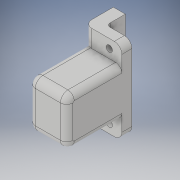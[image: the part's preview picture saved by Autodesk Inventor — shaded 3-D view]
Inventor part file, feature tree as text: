
AUTODESK INVENTOR PART (.ipt)
format: ipt  version: 2019 (Build 230136000, 136)  size: 225,792 bytes
history: native  units: in
note: dims shown in document units (in); Inventor stores cm internally (conversion verified against a paired STEP export)
features: sketch x7, extrude x5, fillet x3, hole x2
ambient origin geometry x8: Origin, YZ Plane, XZ Plane, XY Plane, X Axis, Y Axis, Z Axis, Center Point
bodies: Solid1 (feature_tree)
feature tree (17):
  extrude  "Extrusion1"  Depth=0.75in
  extrude  "Extrusion2"  Depth=0.38in TaperAngle=0.0deg
  extrude  "Extrusion3"  Depth=1.645in
  extrude  "Extrusion4"  Depth=0.35in
  extrude  "Extrusion5"  Depth=0.6in TaperAngle=0.0deg
  hole  "Hole1"  [1 undecoded]
  hole  "Hole2"  [1 undecoded]
  fillet  "Fillet1"  Radius=0.25in
  fillet  "Fillet2"  Radius=0.19in
  fillet  "Fillet3"  Radius=0.19in
  sketch  "Sketch2"  dims[d2=0.75in d3=1.645in]
  sketch  "Sketch3"  dims[d4=1.08in d5=0.0in d8=0.38in d9=0.0in]
  sketch  "Sketch4"  dims[d10=0.51in d11=1.645in]
  sketch  "Sketch6"  dims[d12=0.35in d13=0.35in]
  sketch  "Sketch8"  dims[d14=0.5in d15=0.0in d16=0.6in d17=0.0in]
  sketch  "Sketch9"  dims[d27=0.6in d28=0.0in d29=0.25in]
  sketch  "Sketch10"  dims[d30=0.175in d31=0.175in d32=0.25in d33=0.125in d34=0.75in d35=0.375in d36=0.25in d37=0.5635in d38=0.1in d39=0.8108in d40=0.19in d41=0.19in d42=0.315in d43=0.315in d44=0.125in d45=0.75in d46=0.245in d47=0.075in d48=0.5635in d49=0.1in d50=0.8108in d51=0.15in d52=0.075in d53=0.125in d54=0.75in d55=0.375in]
note: 2 required parameter values undecoded (feature->parameter linkage not recoverable at this tier; creation-order binding heuristic only, values carry confidence <= 0.55)
